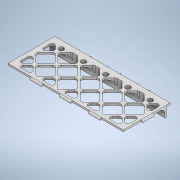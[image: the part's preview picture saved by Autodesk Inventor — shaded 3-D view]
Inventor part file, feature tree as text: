
AUTODESK INVENTOR PART (.ipt)
format: ipt  version: 2020 (Build 240168000, 168)  size: 713,728 bytes
history: native  units: in
note: dims shown in document units (in); Inventor stores cm internally (conversion verified against a paired STEP export)
features: extrude x6, sketch x6, fillet x4
ambient origin geometry x8: Origin, YZ Plane, XZ Plane, XY Plane, X Axis, Y Axis, Z Axis, Center Point
bodies: Solid1 (feature_tree)
feature tree (16):
  extrude  "Extrusion1"  Depth=1.5748in
  extrude  "Extrusion2"  Depth=0.9843in
  extrude  "Extrusion3"  Depth=0.9843in
  fillet  "Fillet3"  Radius=0.1969in
  extrude  "Extrusion4"  Depth=0.3937in
  extrude  "Extrusion5"  Depth=0.3937in
  extrude  "Extrusion6"  Depth=0.1575in
  fillet  "Fillet4"  Radius=0.3937in
  fillet  "Fillet5"  Radius=0.0591in
  fillet  "Fillet6"  Radius=0.1969in
  sketch  "Sketch1"  dims[d0=3.937in d1=1.5748in]
  sketch  "Sketch2"  dims[d2=0.9843in d3=0.9843in]
  sketch  "Sketch3"  dims[d4=0.9843in d5=0.9843in d6=0.1969in]
  sketch  "Sketch4"  dims[d7=0.3937in d8=0.0591in]
  sketch  "Sketch5"  dims[d9=0.1969in d10=0.3937in]
  sketch  "Sketch6"  dims[d11=0.0591in d12=0.1969in d13=0.3937in d14=0.0591in d15=0.1969in d16=0.0591in d17=0.3937in d18=0.1969in d19=0.0591in d20=0.3937in d27=0.0984in d28=0.748in d29=0.748in d30=0.748in d31=0.748in d32=0.748in d33=0.0984in d34=0.0394in d35=1.9685in d37=0.748in d38=0.3937in d40=1.0in d42=135.0deg d43=1.5748in d45=0.748in d46=0.3937in d48=1.0in d50=1.9685in d52=0.748in d53=0.3937in d55=1.0in d57=0.3937in d58=0.0591in d59=0.3937in d60=0.0591in d61=0.3937in d62=0.0591in d63=0.0591in d64=0.0in d67=0.1969in d68=0.0591in d69=0.3937in d70=0.0591in d71=0.0in d72=0.1181in d73=0.0591in d74=0.0591in d75=0.0in d76=0.0787in d77=0.0591in d78=1.0in d79=0.0in d80=0.1181in d81=0.0591in d82=0.0591in d83=0.315in d84=0.0in d85=0.1969in d86=0.0591in d87=0.3937in d88=0.0591in d89=0.0in d90=0.0591in d91=0.0276in d92=0.1575in d44=0.5in]
